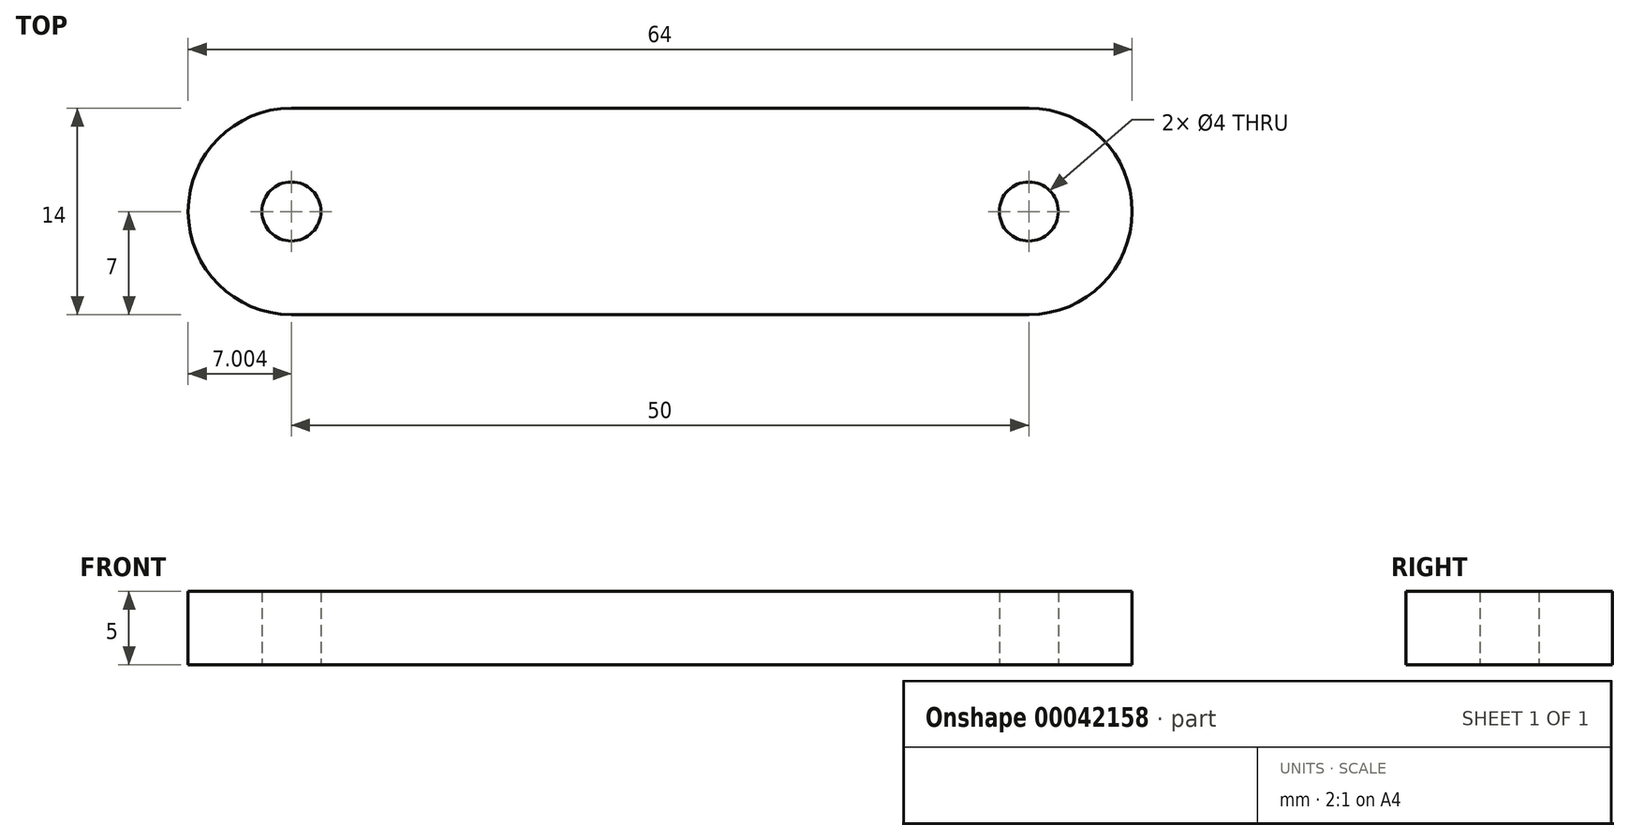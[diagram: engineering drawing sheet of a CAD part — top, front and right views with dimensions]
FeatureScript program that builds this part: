
annotation { "Feature Type Name" : "Feature", "Feature Type Description" : "" }
export const myFeature = defineFeature(function(context is Context, id is Id, definition is map)
    precondition{}
    {
        {
            var Q0;
            Q0=qCreatedBy(makeId("Top.planeOp"),FACE);
            var sketch = newSketch(context, id + "F0", { "sketchPlane" : qUnion([Q0])});
            skCircle(sketch, "E0", {"center": v(-19.02, 0) * mm, "radius": 2 * mm});
            skCircle(sketch, "E1", {"center": v(30.98, 0) * mm, "radius": 2 * mm});
            skLineSegment(sketch, "E2", {"start": v(-19.02, 7) * mm, "end": v(30.98, 7) * mm});
            skLineSegment(sketch, "E3", {"start": v(-19.02, -7) * mm, "end": v(30.98, -7) * mm});
            skArc(sketch, "E4", {"start": v(-19.02, 7) * mm, "mid": v(-26.02, 0) * mm, "end": v(-19.02, -7) * mm});
            skArc(sketch, "E5", {"start": v(30.98, 7) * mm, "mid": v(37.98, 0) * mm, "end": v(30.98, -7) * mm});
            skSolve(sketch);
        }
        {
            var Q0;
            Q0=makeQuery(id+"F0.imprint","IMPRINT",FACE,{"disambiguationData":[TD([[makeQuery(id+"F0.imprint","IMPRINT",EDGE,{"derivedFrom":sQuery(id+"F0.wireOp",EDGE,"E0")}),-1.0]])]});
            extrude(context, id + "F1", {"entities" : qUnion([Q0]), "depth" : 5 * mm});
        }
    });
